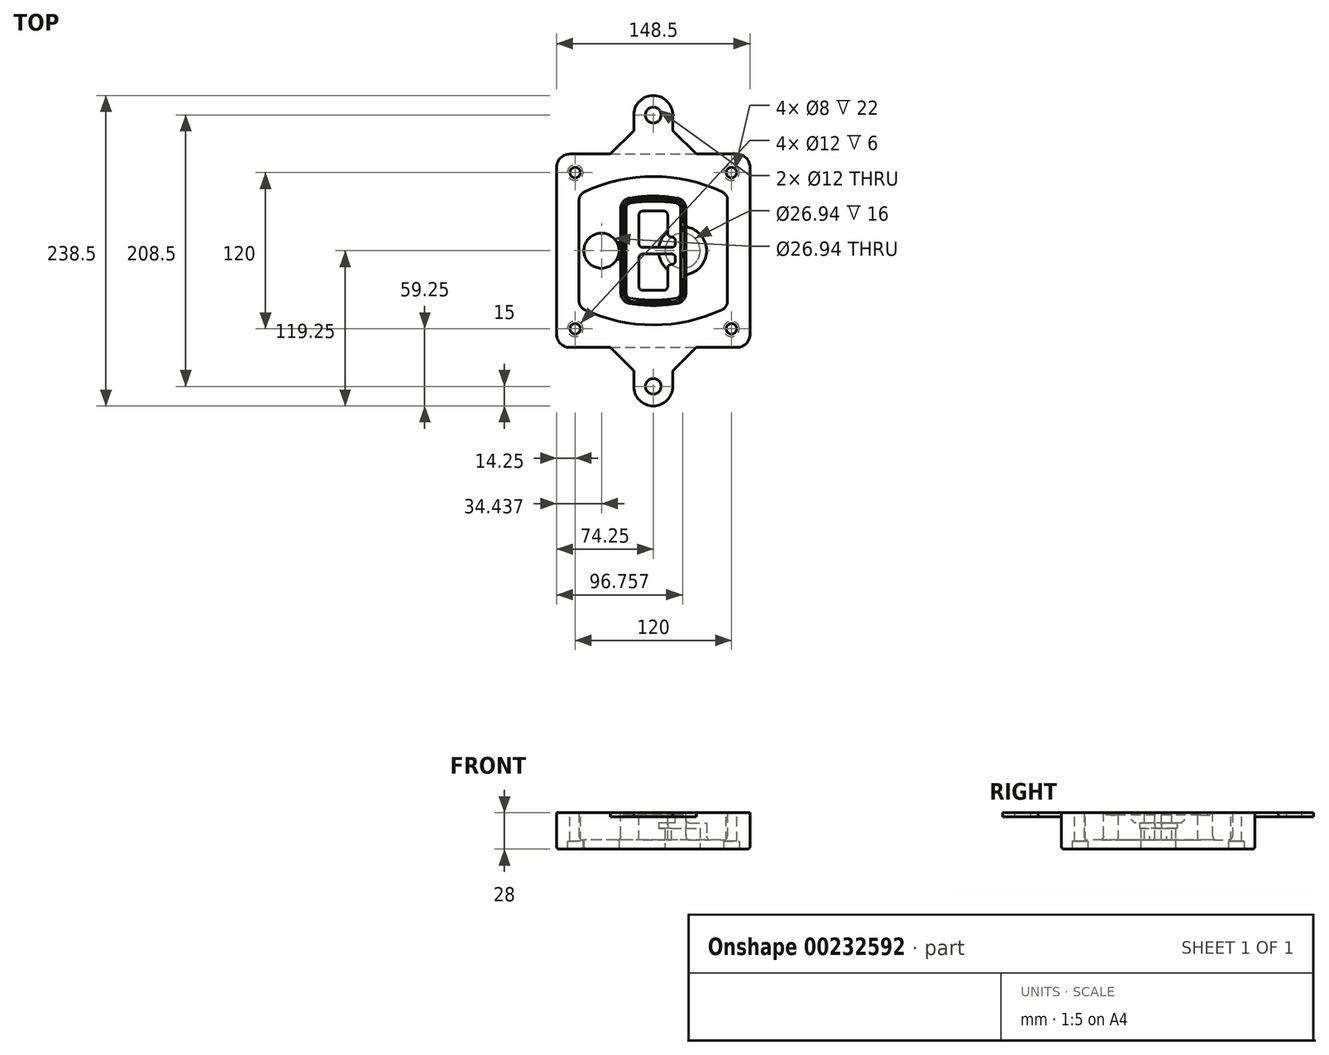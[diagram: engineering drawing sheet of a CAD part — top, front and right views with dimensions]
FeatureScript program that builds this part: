
annotation { "Feature Type Name" : "Feature", "Feature Type Description" : "" }
export const myFeature = defineFeature(function(context is Context, id is Id, definition is map)
    precondition{}
    {
        {
            var Q0;
            Q0=qCreatedBy(makeId("Top.planeOp"),FACE);
            var sketch = newSketch(context, id + "F0", { "sketchPlane" : qUnion([Q0])});
            skPoint(sketch, "E0.rect.middle", {"position": v(0, 0) * mm});
            skLineSegment(sketch, "E1.bottom", {"start": v(-64.25, -74.25) * mm, "end": v(64.25, -74.25) * mm});
            skLineSegment(sketch, "E1.top", {"start": v(-64.25, 74.25) * mm, "end": v(64.25, 74.25) * mm});
            skLineSegment(sketch, "E1.left", {"start": v(-74.25, -64.25) * mm, "end": v(-74.25, 64.25) * mm});
            skLineSegment(sketch, "E1.right", {"start": v(74.25, -64.25) * mm, "end": v(74.25, 64.25) * mm});
            skLineSegment(sketch, "E2", {"start": v(-74.25, 74.25) * mm, "end": v(74.25, -74.25) * mm, "construction": true});
            skLineSegment(sketch, "E3", {"start": v(74.25, 74.25) * mm, "end": v(-74.25, -74.25) * mm, "construction": true});
            skCircle(sketch, "E4", {"center": v(-60, 60) * mm, "radius": 4 * mm});
            skCircle(sketch, "E5", {"center": v(60, 60) * mm, "radius": 4 * mm});
            skCircle(sketch, "E6", {"center": v(60, -60) * mm, "radius": 4 * mm});
            skCircle(sketch, "E7", {"center": v(-60, -60) * mm, "radius": 4 * mm});
            skLineSegment(sketch, "E8", {"start": v(-60, 60) * mm, "end": v(60, 60) * mm, "construction": true});
            skLineSegment(sketch, "E9", {"start": v(60, 60) * mm, "end": v(60, -60) * mm, "construction": true});
            skLineSegment(sketch, "E10", {"start": v(60, -60) * mm, "end": v(-60, -60) * mm, "construction": true});
            skLineSegment(sketch, "E11", {"start": v(-60, -60) * mm, "end": v(-60, 60) * mm, "construction": true});
            skLineSegment(sketch, "E12", {"start": v(-60, 38.83) * mm, "end": v(-60, -38.83) * mm});
            skLineSegment(sketch, "E13", {"start": v(60, 38.83) * mm, "end": v(60, -38.83) * mm});
            skArc(sketch, "E14", {"start": v(54.26, 47.88) * mm, "mid": v(0, 60) * mm, "end": v(-54.26, 47.88) * mm});
            skArc(sketch, "E15", {"start": v(-54.26, -47.88) * mm, "mid": v(0, -60) * mm, "end": v(54.26, -47.88) * mm});
            skLineSegment(sketch, "E16", {"start": v(-60, 0) * mm, "end": v(60, 0) * mm, "construction": true});
            skPoint(sketch, "E17.visualSharp", {"position": v(-60, -45) * mm});
            skArc(sketch, "E17.filletArc", {"start": v(-60, -38.83) * mm, "mid": v(-58.44, -44.2) * mm, "end": v(-54.26, -47.88) * mm});
            skPoint(sketch, "E18.visualSharp", {"position": v(-60, 45) * mm});
            skArc(sketch, "E18.filletArc", {"start": v(-54.26, 47.88) * mm, "mid": v(-58.44, 44.2) * mm, "end": v(-60, 38.83) * mm});
            skPoint(sketch, "E19.visualSharp", {"position": v(60, 45) * mm});
            skArc(sketch, "E19.filletArc", {"start": v(60, 38.83) * mm, "mid": v(58.44, 44.2) * mm, "end": v(54.26, 47.88) * mm});
            skPoint(sketch, "E20.visualSharp", {"position": v(60, -45) * mm});
            skArc(sketch, "E20.filletArc", {"start": v(54.26, -47.88) * mm, "mid": v(58.44, -44.2) * mm, "end": v(60, -38.83) * mm});
            skPoint(sketch, "E21.visualSharp", {"position": v(-74.25, 74.25) * mm});
            skArc(sketch, "E21.filletArc", {"start": v(-64.25, 74.25) * mm, "mid": v(-71.32, 71.32) * mm, "end": v(-74.25, 64.25) * mm});
            skPoint(sketch, "E22.visualSharp", {"position": v(74.25, 74.25) * mm});
            skArc(sketch, "E22.filletArc", {"start": v(74.25, 64.25) * mm, "mid": v(71.32, 71.32) * mm, "end": v(64.25, 74.25) * mm});
            skPoint(sketch, "E23.visualSharp", {"position": v(74.25, -74.25) * mm});
            skArc(sketch, "E23.filletArc", {"start": v(64.25, -74.25) * mm, "mid": v(71.32, -71.32) * mm, "end": v(74.25, -64.25) * mm});
            skPoint(sketch, "E24.visualSharp", {"position": v(-74.25, -74.25) * mm});
            skArc(sketch, "E24.filletArc", {"start": v(-74.25, -64.25) * mm, "mid": v(-71.32, -71.32) * mm, "end": v(-64.25, -74.25) * mm});
            skArc(sketch, "E25.0", {"start": v(57, 38.83) * mm, "mid": v(55.9, 42.58) * mm, "end": v(52.98, 45.17) * mm});
            skLineSegment(sketch, "E25.1", {"start": v(57, 38.83) * mm, "end": v(57, -38.83) * mm});
            skArc(sketch, "E25.2", {"start": v(52.98, -45.17) * mm, "mid": v(55.9, -42.58) * mm, "end": v(57, -38.83) * mm});
            skArc(sketch, "E25.3", {"start": v(-52.98, -45.17) * mm, "mid": v(0, -57) * mm, "end": v(52.98, -45.17) * mm});
            skArc(sketch, "E25.4", {"start": v(-57, -38.83) * mm, "mid": v(-55.9, -42.58) * mm, "end": v(-52.98, -45.17) * mm});
            skArc(sketch, "E25.5", {"start": v(52.98, 45.17) * mm, "mid": v(0, 57) * mm, "end": v(-52.98, 45.17) * mm});
            skLineSegment(sketch, "E25.6", {"start": v(-57, 38.83) * mm, "end": v(-57, -38.83) * mm});
            skArc(sketch, "E25.7", {"start": v(-52.98, 45.17) * mm, "mid": v(-55.9, 42.58) * mm, "end": v(-57, 38.83) * mm});
            skArc(sketch, "E26.0", {"start": v(-55.96, 51.5) * mm, "mid": v(-61.82, 46.33) * mm, "end": v(-64, 38.83) * mm});
            skArc(sketch, "E26.1", {"start": v(55.96, 51.5) * mm, "mid": v(0, 64) * mm, "end": v(-55.96, 51.5) * mm});
            skArc(sketch, "E26.2", {"start": v(64, 38.83) * mm, "mid": v(61.82, 46.33) * mm, "end": v(55.96, 51.5) * mm});
            skLineSegment(sketch, "E26.3", {"start": v(64, 38.83) * mm, "end": v(64, -38.83) * mm});
            skArc(sketch, "E26.4", {"start": v(55.96, -51.5) * mm, "mid": v(61.82, -46.33) * mm, "end": v(64, -38.83) * mm});
            skLineSegment(sketch, "E26.5", {"start": v(-64, 38.83) * mm, "end": v(-64, -38.83) * mm});
            skArc(sketch, "E26.6", {"start": v(-55.96, -51.5) * mm, "mid": v(0, -64) * mm, "end": v(55.96, -51.5) * mm});
            skArc(sketch, "E26.7", {"start": v(-64, -38.83) * mm, "mid": v(-61.82, -46.33) * mm, "end": v(-55.96, -51.5) * mm});
            skSolve(sketch);
        }
        {
            var Q0;
            Q0=makeQuery(id+"F0.imprint","IMPRINT",FACE,{"disambiguationData":[TD([[makeQuery(id+"F0.imprint","IMPRINT",EDGE,{"derivedFrom":sQuery(id+"F0.wireOp",EDGE,"E1.bottom")}),1.0]])]});
            var Q1;
            Q1=makeQuery(id+"F0.imprint","IMPRINT",FACE,{"disambiguationData":[TD([[makeQuery(id+"F0.imprint","IMPRINT",EDGE,{"derivedFrom":sQuery(id+"F0.wireOp",EDGE,"E12")}),1.0]])]});
            var Q2;
            Q2=makeQuery(id+"F0.imprint","IMPRINT",FACE,{"disambiguationData":[TD([[makeQuery(id+"F0.imprint","IMPRINT",EDGE,{"derivedFrom":sQuery(id+"F0.wireOp",EDGE,"E25.0")}),1.0]])]});
            var Q3;
            Q3=makeQuery(id+"F0.imprint","IMPRINT",FACE,{"disambiguationData":[TD([[makeQuery(id+"F0.imprint","IMPRINT",EDGE,{"derivedFrom":sQuery(id+"F0.wireOp",EDGE,"E12")}),-1.0]])]});
            extrude(context, id + "F1", {"entities" : qUnion([Q0, Q1, Q2, Q3]), "oppositeDirection" : true, "depth" : 25 * mm});
        }
        {
            var Q0;
            Q0=makeQuery(id+"F0.imprint","IMPRINT",FACE,{"disambiguationData":[TD([[makeQuery(id+"F0.imprint","IMPRINT",EDGE,{"derivedFrom":sQuery(id+"F0.wireOp",EDGE,"E12")}),1.0]])]});
            extrude(context, id + "F2", {"entities" : qUnion([Q0]), "operationType" : NewBodyOperationType.ADD, "depth" : 3 * mm});
        }
        {
            var Q0;
            Q0=makeQuery(id+"F0.imprint","IMPRINT",FACE,{"disambiguationData":[TD([[makeQuery(id+"F0.imprint","IMPRINT",EDGE,{"derivedFrom":sQuery(id+"F0.wireOp",EDGE,"E25.0")}),1.0]])]});
            extrude(context, id + "F3", {"entities" : qUnion([Q0]), "operationType" : NewBodyOperationType.REMOVE, "oppositeDirection" : true, "depth" : 18 * mm});
        }
        {
            var Q0;
            Q0=makeQuery(id+"F2.opExtrude","CAP_FACE",FACE,{"disambiguationData":[OSD([sQuery(id+"F0.wireOp",EDGE,"E12"),sQuery(id+"F0.wireOp",EDGE,"E13"),sQuery(id+"F0.wireOp",EDGE,"E14"),sQuery(id+"F0.wireOp",EDGE,"E15"),sQuery(id+"F0.wireOp",EDGE,"E17.filletArc"),sQuery(id+"F0.wireOp",EDGE,"E18.filletArc"),sQuery(id+"F0.wireOp",EDGE,"E19.filletArc"),sQuery(id+"F0.wireOp",EDGE,"E20.filletArc"),sQuery(id+"F0.wireOp",EDGE,"E25.0"),sQuery(id+"F0.wireOp",EDGE,"E25.1"),sQuery(id+"F0.wireOp",EDGE,"E25.2"),sQuery(id+"F0.wireOp",EDGE,"E25.3"),sQuery(id+"F0.wireOp",EDGE,"E25.4"),sQuery(id+"F0.wireOp",EDGE,"E25.5"),sQuery(id+"F0.wireOp",EDGE,"E25.6"),sQuery(id+"F0.wireOp",EDGE,"E25.7")])],"isStart":false});
            var sketch = newSketch(context, id + "F4", { "sketchPlane" : qUnion([Q0])});
            skArc(sketch, "E27.0", {"start": v(-18.34, -40.45) * mm, "mid": v(0, -42) * mm, "end": v(18.34, -40.45) * mm});
            skArc(sketch, "E28.0", {"start": v(18.34, 40.45) * mm, "mid": v(0, 42) * mm, "end": v(-18.34, 40.45) * mm});
            skLineSegment(sketch, "E29", {"start": v(-25, 32.57) * mm, "end": v(-25, -32.57) * mm});
            skLineSegment(sketch, "E30", {"start": v(25, 32.57) * mm, "end": v(25, -32.57) * mm});
            skLineSegment(sketch, "E31", {"start": v(-25, 39.1) * mm, "end": v(25, 39.1) * mm, "construction": true});
            skLineSegment(sketch, "E32", {"start": v(-25, -39.1) * mm, "end": v(25, -39.1) * mm, "construction": true});
            skPoint(sketch, "E33.visualSharp", {"position": v(-25, 39.1) * mm});
            skArc(sketch, "E33.filletArc", {"start": v(-18.34, 40.45) * mm, "mid": v(-23.11, 37.73) * mm, "end": v(-25, 32.57) * mm});
            skPoint(sketch, "E34.visualSharp", {"position": v(25, 39.1) * mm});
            skArc(sketch, "E34.filletArc", {"start": v(25, 32.57) * mm, "mid": v(23.11, 37.73) * mm, "end": v(18.34, 40.45) * mm});
            skPoint(sketch, "E35.visualSharp", {"position": v(25, -39.1) * mm});
            skArc(sketch, "E35.filletArc", {"start": v(18.34, -40.45) * mm, "mid": v(23.11, -37.73) * mm, "end": v(25, -32.57) * mm});
            skPoint(sketch, "E36.visualSharp", {"position": v(-25, -39.1) * mm});
            skArc(sketch, "E36.filletArc", {"start": v(-25, -32.57) * mm, "mid": v(-23.11, -37.73) * mm, "end": v(-18.34, -40.45) * mm});
            skArc(sketch, "E37.0", {"start": v(52.98, 45.17) * mm, "mid": v(0, 57) * mm, "end": v(-52.98, 45.17) * mm});
            skArc(sketch, "E37.1", {"start": v(-52.98, 45.17) * mm, "mid": v(-55.9, 42.58) * mm, "end": v(-57, 38.83) * mm});
            skLineSegment(sketch, "E37.2", {"start": v(-57, 38.83) * mm, "end": v(-57, -38.83) * mm});
            skArc(sketch, "E37.3", {"start": v(-57, -38.83) * mm, "mid": v(-55.9, -42.58) * mm, "end": v(-52.98, -45.17) * mm});
            skArc(sketch, "E37.4", {"start": v(-52.98, -45.17) * mm, "mid": v(0, -57) * mm, "end": v(52.98, -45.17) * mm});
            skArc(sketch, "E37.5", {"start": v(52.98, -45.17) * mm, "mid": v(55.9, -42.58) * mm, "end": v(57, -38.83) * mm});
            skLineSegment(sketch, "E37.6", {"start": v(57, 38.83) * mm, "end": v(57, -38.83) * mm});
            skArc(sketch, "E37.7", {"start": v(57, 38.83) * mm, "mid": v(55.9, 42.58) * mm, "end": v(52.98, 45.17) * mm});
            skLineSegment(sketch, "E38.0", {"start": v(23, 32.57) * mm, "end": v(23, -32.57) * mm});
            skArc(sketch, "E38.1", {"start": v(18, -38.48) * mm, "mid": v(21.58, -36.44) * mm, "end": v(23, -32.57) * mm});
            skArc(sketch, "E38.2", {"start": v(-18, -38.48) * mm, "mid": v(0, -40) * mm, "end": v(18, -38.48) * mm});
            skArc(sketch, "E38.3", {"start": v(-23, -32.57) * mm, "mid": v(-21.58, -36.44) * mm, "end": v(-18, -38.48) * mm});
            skLineSegment(sketch, "E38.4", {"start": v(-23, 32.57) * mm, "end": v(-23, -32.57) * mm});
            skArc(sketch, "E38.5", {"start": v(23, 32.57) * mm, "mid": v(21.58, 36.44) * mm, "end": v(18, 38.48) * mm});
            skArc(sketch, "E38.6", {"start": v(-18, 38.48) * mm, "mid": v(-21.58, 36.44) * mm, "end": v(-23, 32.57) * mm});
            skArc(sketch, "E38.7", {"start": v(18, 38.48) * mm, "mid": v(0, 40) * mm, "end": v(-18, 38.48) * mm});
            skArc(sketch, "E39.0", {"start": v(21, 32.57) * mm, "mid": v(20.06, 35.15) * mm, "end": v(17.67, 36.5) * mm});
            skLineSegment(sketch, "E39.1", {"start": v(21, 32.57) * mm, "end": v(21, -32.57) * mm});
            skArc(sketch, "E39.2", {"start": v(17.67, -36.5) * mm, "mid": v(20.06, -35.15) * mm, "end": v(21, -32.57) * mm});
            skArc(sketch, "E39.3", {"start": v(-17.67, -36.5) * mm, "mid": v(0, -38) * mm, "end": v(17.67, -36.5) * mm});
            skArc(sketch, "E39.4", {"start": v(-21, -32.57) * mm, "mid": v(-20.06, -35.15) * mm, "end": v(-17.67, -36.5) * mm});
            skArc(sketch, "E39.5", {"start": v(17.67, 36.5) * mm, "mid": v(0, 38) * mm, "end": v(-17.67, 36.5) * mm});
            skLineSegment(sketch, "E39.6", {"start": v(-21, 32.57) * mm, "end": v(-21, -32.57) * mm});
            skArc(sketch, "E39.7", {"start": v(-17.67, 36.5) * mm, "mid": v(-20.06, 35.15) * mm, "end": v(-21, 32.57) * mm});
            skLineSegment(sketch, "E40", {"start": v(-25, 0) * mm, "end": v(25, 0) * mm, "construction": true});
            skLineSegment(sketch, "E41", {"start": v(-11, 5.5) * mm, "end": v(-11, 27.5) * mm});
            skLineSegment(sketch, "E42", {"start": v(-8, 30.5) * mm, "end": v(8, 30.5) * mm});
            skLineSegment(sketch, "E43", {"start": v(11, 27.5) * mm, "end": v(11, 13.5) * mm});
            skLineSegment(sketch, "E44", {"start": v(14, 10.5) * mm, "end": v(14, 10.5) * mm});
            skLineSegment(sketch, "E45", {"start": v(17, 7.5) * mm, "end": v(17, 5.5) * mm});
            skLineSegment(sketch, "E46", {"start": v(14, 2.5) * mm, "end": v(-8, 2.5) * mm});
            skPoint(sketch, "E47.visualSharp", {"position": v(-11, 30.5) * mm});
            skArc(sketch, "E47.filletArc", {"start": v(-8, 30.5) * mm, "mid": v(-10.12, 29.62) * mm, "end": v(-11, 27.5) * mm});
            skPoint(sketch, "E48.visualSharp", {"position": v(11, 30.5) * mm});
            skArc(sketch, "E48.filletArc", {"start": v(11, 27.5) * mm, "mid": v(10.12, 29.62) * mm, "end": v(8, 30.5) * mm});
            skPoint(sketch, "E49.visualSharp", {"position": v(11, 10.5) * mm});
            skArc(sketch, "E49.filletArc", {"start": v(11, 13.5) * mm, "mid": v(11.88, 11.38) * mm, "end": v(14, 10.5) * mm});
            skPoint(sketch, "E50.visualSharp", {"position": v(17, 10.5) * mm});
            skArc(sketch, "E50.filletArc", {"start": v(17, 7.5) * mm, "mid": v(16.12, 9.62) * mm, "end": v(14, 10.5) * mm});
            skPoint(sketch, "E51.visualSharp", {"position": v(17, 2.5) * mm});
            skArc(sketch, "E51.filletArc", {"start": v(14, 2.5) * mm, "mid": v(16.12, 3.38) * mm, "end": v(17, 5.5) * mm});
            skPoint(sketch, "E52.visualSharp", {"position": v(-11, 2.5) * mm});
            skArc(sketch, "E52.filletArc", {"start": v(-11, 5.5) * mm, "mid": v(-10.12, 3.38) * mm, "end": v(-8, 2.5) * mm});
            skLineSegment(sketch, "E53.0.MirrorCS", {"start": v(14, -2.5) * mm, "end": v(-8, -2.5) * mm});
            skArc(sketch, "E54.0.MirrorCS", {"start": v(-11, -5.5) * mm, "mid": v(-10.12, -3.38) * mm, "end": v(-8, -2.5) * mm});
            skLineSegment(sketch, "E55.0.MirrorCS", {"start": v(-11, -5.5) * mm, "end": v(-11, -27.5) * mm});
            skArc(sketch, "E56.0.MirrorCS", {"start": v(-8, -30.5) * mm, "mid": v(-10.12, -29.62) * mm, "end": v(-11, -27.5) * mm});
            skLineSegment(sketch, "E57.0.MirrorCS", {"start": v(-8, -30.5) * mm, "end": v(8, -30.5) * mm});
            skArc(sketch, "E58.0.MirrorCS", {"start": v(11, -27.5) * mm, "mid": v(10.12, -29.62) * mm, "end": v(8, -30.5) * mm});
            skLineSegment(sketch, "E59.0.MirrorCS", {"start": v(11, -27.5) * mm, "end": v(11, -13.5) * mm});
            skArc(sketch, "E60.0.MirrorCS", {"start": v(11, -13.5) * mm, "mid": v(11.88, -11.38) * mm, "end": v(14, -10.5) * mm});
            skArc(sketch, "E61.0.MirrorCS", {"start": v(17, -7.5) * mm, "mid": v(16.12, -9.62) * mm, "end": v(14, -10.5) * mm});
            skLineSegment(sketch, "E62.0.MirrorCS", {"start": v(17, -7.5) * mm, "end": v(17, -5.5) * mm});
            skArc(sketch, "E63.0.MirrorCS", {"start": v(14, -2.5) * mm, "mid": v(16.12, -3.38) * mm, "end": v(17, -5.5) * mm});
            skSolve(sketch);
        }
        {
            var Q0;
            Q0=makeQuery(id+"F4.imprint","IMPRINT",FACE,{"disambiguationData":[TD([[makeQuery(id+"F4.imprint","IMPRINT",EDGE,{"derivedFrom":sQuery(id+"F4.wireOp",EDGE,"E27.0")}),1.0]])]});
            var Q1;
            Q1=makeQuery(id+"F4.imprint","IMPRINT",FACE,{"disambiguationData":[TD([[makeQuery(id+"F4.imprint","IMPRINT",EDGE,{"derivedFrom":sQuery(id+"F4.wireOp",EDGE,"E38.0")}),-1.0]])]});
            var Q2;
            Q2=makeQuery(id+"F4.imprint","IMPRINT",FACE,{"disambiguationData":[TD([[makeQuery(id+"F4.imprint","IMPRINT",EDGE,{"derivedFrom":sQuery(id+"F4.wireOp",EDGE,"E39.0")}),1.0]])]});
            extrude(context, id + "F5", {"entities" : qUnion([Q0, Q1, Q2]), "operationType" : NewBodyOperationType.ADD, "endBound" : BoundingType.UP_TO_NEXT, "oppositeDirection" : true, "depth" : 25 * mm});
        }
        {
            var Q0;
            Q0=makeQuery(id+"F4.imprint","IMPRINT",FACE,{"disambiguationData":[TD([[makeQuery(id+"F4.imprint","IMPRINT",EDGE,{"derivedFrom":sQuery(id+"F4.wireOp",EDGE,"E38.0")}),-1.0]])]});
            extrude(context, id + "F6", {"entities" : qUnion([Q0]), "operationType" : NewBodyOperationType.REMOVE, "oppositeDirection" : true, "depth" : 2 * mm});
        }
        {
            var Q0;
            Q0=makeQuery(id+"F1.opExtrude","CAP_FACE",FACE,{"disambiguationData":[OSD([sQuery(id+"F0.wireOp",EDGE,"E1.bottom"),sQuery(id+"F0.wireOp",EDGE,"E1.top"),sQuery(id+"F0.wireOp",EDGE,"E1.left"),sQuery(id+"F0.wireOp",EDGE,"E1.right"),sQuery(id+"F0.wireOp",EDGE,"E4"),sQuery(id+"F0.wireOp",EDGE,"E5"),sQuery(id+"F0.wireOp",EDGE,"E6"),sQuery(id+"F0.wireOp",EDGE,"E7"),sQuery(id+"F0.wireOp",EDGE,"E21.filletArc"),sQuery(id+"F0.wireOp",EDGE,"E22.filletArc"),sQuery(id+"F0.wireOp",EDGE,"E23.filletArc"),sQuery(id+"F0.wireOp",EDGE,"E24.filletArc")])],"isStart":false});
            var sketch = newSketch(context, id + "F7", { "sketchPlane" : qUnion([Q0])});
            skCircle(sketch, "E64", {"center": v(22.5, 0) * mm, "radius": 13.47 * mm});
            skCircle(sketch, "E65", {"center": v(-39.81, 0) * mm, "radius": 13.47 * mm});
            skLineSegment(sketch, "E66", {"start": v(74.25, 0) * mm, "end": v(-74.25, 0) * mm});
            skCircle(sketch, "E67", {"center": v(22.5, 0) * mm, "radius": 18.47 * mm});
            skCircle(sketch, "E68", {"center": v(60, -60) * mm, "radius": 6 * mm});
            skCircle(sketch, "E69", {"center": v(-60, -60) * mm, "radius": 6 * mm});
            skCircle(sketch, "E70", {"center": v(-60, 60) * mm, "radius": 6 * mm});
            skCircle(sketch, "E71", {"center": v(60, 60) * mm, "radius": 6 * mm});
            skSolve(sketch);
        }
        {
            var Q0;
            {var subQ1=sQuery(id+"F7.wireOp",EDGE,"E66");var subQ4=sQuery(id+"F7.wireOp",EDGE,"E64");var subQ6=makeQuery(id+"F7.imprint","INTERSECT",VERTEX,{"disambiguationData":[OD(0.0)],"derivedFrom":[subQ4,subQ1]});Q0=makeQuery(id+"F7.imprint","IMPRINT",FACE,{"disambiguationData":[TD([[makeQuery(id+"F7.imprint","IMPRINT",EDGE,{"disambiguationData":[TD([[subQ6,-1.0]])],"derivedFrom":subQ4}),-1.0]])]});}
            var Q1;
            {var subQ0=sQuery(id+"F7.wireOp",EDGE,"E66");var subQ1=sQuery(id+"F7.wireOp",EDGE,"E64");var subQ3=makeQuery(id+"F7.imprint","INTERSECT",VERTEX,{"disambiguationData":[OD(0.0)],"derivedFrom":[subQ1,subQ0]});Q1=makeQuery(id+"F7.imprint","IMPRINT",FACE,{"disambiguationData":[TD([[makeQuery(id+"F7.imprint","IMPRINT",EDGE,{"disambiguationData":[TD([[subQ3,-1.0]])],"derivedFrom":subQ1}),1.0]])]});}
            var Q2;
            {var subQ0=sQuery(id+"F7.wireOp",EDGE,"E66");var subQ1=sQuery(id+"F7.wireOp",EDGE,"E64");var subQ3=makeQuery(id+"F7.imprint","INTERSECT",VERTEX,{"disambiguationData":[OD(0.0)],"derivedFrom":[subQ1,subQ0]});Q2=makeQuery(id+"F7.imprint","IMPRINT",FACE,{"disambiguationData":[TD([[makeQuery(id+"F7.imprint","IMPRINT",EDGE,{"disambiguationData":[TD([[subQ3,1.0]])],"derivedFrom":subQ1}),1.0]])]});}
            var Q3;
            {var subQ1=sQuery(id+"F7.wireOp",EDGE,"E66");var subQ4=sQuery(id+"F7.wireOp",EDGE,"E64");var subQ6=makeQuery(id+"F7.imprint","INTERSECT",VERTEX,{"disambiguationData":[OD(0.0)],"derivedFrom":[subQ4,subQ1]});Q3=makeQuery(id+"F7.imprint","IMPRINT",FACE,{"disambiguationData":[TD([[makeQuery(id+"F7.imprint","IMPRINT",EDGE,{"disambiguationData":[TD([[subQ6,1.0]])],"derivedFrom":subQ4}),-1.0]])]});}
            extrude(context, id + "F8", {"entities" : qUnion([Q0, Q1, Q2, Q3]), "operationType" : NewBodyOperationType.ADD, "oppositeDirection" : true, "depth" : 20 * mm});
        }
        {
            var Q0;
            {var subQ0=sQuery(id+"F7.wireOp",EDGE,"E66");var subQ1=sQuery(id+"F7.wireOp",EDGE,"E64");var subQ3=makeQuery(id+"F7.imprint","INTERSECT",VERTEX,{"disambiguationData":[OD(0.0)],"derivedFrom":[subQ1,subQ0]});Q0=makeQuery(id+"F7.imprint","IMPRINT",FACE,{"disambiguationData":[TD([[makeQuery(id+"F7.imprint","IMPRINT",EDGE,{"disambiguationData":[TD([[subQ3,-1.0]])],"derivedFrom":subQ1}),1.0]])]});}
            var Q1;
            {var subQ0=sQuery(id+"F7.wireOp",EDGE,"E66");var subQ1=sQuery(id+"F7.wireOp",EDGE,"E64");var subQ3=makeQuery(id+"F7.imprint","INTERSECT",VERTEX,{"disambiguationData":[OD(0.0)],"derivedFrom":[subQ1,subQ0]});Q1=makeQuery(id+"F7.imprint","IMPRINT",FACE,{"disambiguationData":[TD([[makeQuery(id+"F7.imprint","IMPRINT",EDGE,{"disambiguationData":[TD([[subQ3,1.0]])],"derivedFrom":subQ1}),1.0]])]});}
            extrude(context, id + "F9", {"entities" : qUnion([Q0, Q1]), "operationType" : NewBodyOperationType.REMOVE, "oppositeDirection" : true, "depth" : 16 * mm});
        }
        {
            var Q0;
            {var subQ0=sQuery(id+"F7.wireOp",EDGE,"E66");var subQ1=sQuery(id+"F7.wireOp",EDGE,"E65");var subQ3=makeQuery(id+"F7.imprint","INTERSECT",VERTEX,{"disambiguationData":[OD(0.0)],"derivedFrom":[subQ1,subQ0]});Q0=makeQuery(id+"F7.imprint","IMPRINT",FACE,{"disambiguationData":[TD([[makeQuery(id+"F7.imprint","IMPRINT",EDGE,{"disambiguationData":[TD([[subQ3,-1.0]])],"derivedFrom":subQ1}),1.0]])]});}
            var Q1;
            {var subQ0=sQuery(id+"F7.wireOp",EDGE,"E66");var subQ1=sQuery(id+"F7.wireOp",EDGE,"E65");var subQ3=makeQuery(id+"F7.imprint","INTERSECT",VERTEX,{"disambiguationData":[OD(0.0)],"derivedFrom":[subQ1,subQ0]});Q1=makeQuery(id+"F7.imprint","IMPRINT",FACE,{"disambiguationData":[TD([[makeQuery(id+"F7.imprint","IMPRINT",EDGE,{"disambiguationData":[TD([[subQ3,1.0]])],"derivedFrom":subQ1}),1.0]])]});}
            extrude(context, id + "F10", {"entities" : qUnion([Q0, Q1]), "operationType" : NewBodyOperationType.REMOVE, "oppositeDirection" : true, "depth" : 25 * mm});
        }
        {
            var Q0;
            Q0=makeQuery(id+"F7.imprint","IMPRINT",FACE,{"disambiguationData":[TD([[makeQuery(id+"F7.imprint","IMPRINT",EDGE,{"derivedFrom":sQuery(id+"F7.wireOp",EDGE,"E68")}),1.0]])]});
            var Q1;
            Q1=makeQuery(id+"F7.imprint","IMPRINT",FACE,{"disambiguationData":[TD([[makeQuery(id+"F7.imprint","IMPRINT",EDGE,{"derivedFrom":makeQuery(id+"F1.opExtrude","CAP_EDGE",EDGE,{"disambiguationData":[OSD([sQuery(id+"F0.wireOp",EDGE,"E5")])],"isStart":false})}),-1.0]])]});
            var Q2;
            Q2=makeQuery(id+"F7.imprint","IMPRINT",FACE,{"disambiguationData":[TD([[makeQuery(id+"F7.imprint","IMPRINT",EDGE,{"derivedFrom":sQuery(id+"F7.wireOp",EDGE,"E69")}),1.0]])]});
            var Q3;
            Q3=makeQuery(id+"F7.imprint","IMPRINT",FACE,{"disambiguationData":[TD([[makeQuery(id+"F7.imprint","IMPRINT",EDGE,{"derivedFrom":makeQuery(id+"F1.opExtrude","CAP_EDGE",EDGE,{"disambiguationData":[OSD([sQuery(id+"F0.wireOp",EDGE,"E4")])],"isStart":false})}),-1.0]])]});
            var Q4;
            Q4=makeQuery(id+"F7.imprint","IMPRINT",FACE,{"disambiguationData":[TD([[makeQuery(id+"F7.imprint","IMPRINT",EDGE,{"derivedFrom":sQuery(id+"F7.wireOp",EDGE,"E70")}),1.0]])]});
            var Q5;
            Q5=makeQuery(id+"F7.imprint","IMPRINT",FACE,{"disambiguationData":[TD([[makeQuery(id+"F7.imprint","IMPRINT",EDGE,{"derivedFrom":makeQuery(id+"F1.opExtrude","CAP_EDGE",EDGE,{"disambiguationData":[OSD([sQuery(id+"F0.wireOp",EDGE,"E7")])],"isStart":false})}),-1.0]])]});
            var Q6;
            Q6=makeQuery(id+"F7.imprint","IMPRINT",FACE,{"disambiguationData":[TD([[makeQuery(id+"F7.imprint","IMPRINT",EDGE,{"derivedFrom":sQuery(id+"F7.wireOp",EDGE,"E71")}),1.0]])]});
            var Q7;
            Q7=makeQuery(id+"F7.imprint","IMPRINT",FACE,{"disambiguationData":[TD([[makeQuery(id+"F7.imprint","IMPRINT",EDGE,{"derivedFrom":makeQuery(id+"F1.opExtrude","CAP_EDGE",EDGE,{"disambiguationData":[OSD([sQuery(id+"F0.wireOp",EDGE,"E6")])],"isStart":false})}),-1.0]])]});
            extrude(context, id + "F11", {"entities" : qUnion([Q0, Q1, Q2, Q3, Q4, Q5, Q6, Q7]), "operationType" : NewBodyOperationType.REMOVE, "oppositeDirection" : true, "depth" : 6 * mm});
        }
        {
            var Q0;
            Q0=makeQuery(id+"F9.boolean.opBoolean","COPY",FACE,{"derivedFrom":makeQuery(id+"F9.opExtrude","CAP_FACE",FACE,{"disambiguationData":[OSD([sQuery(id+"F7.wireOp",EDGE,"E64")])],"isStart":false})});
            var sketch = newSketch(context, id + "F12", { "sketchPlane" : qUnion([Q0])});
            skArc(sketch, "E72.0", {"start": v(11, 14.45) * mm, "mid": v(6.45, 9.13) * mm, "end": v(4.2, 2.5) * mm});
            skArc(sketch, "E72.1", {"start": v(4.2, -2.5) * mm, "mid": v(6.45, -9.13) * mm, "end": v(11, -14.45) * mm});
            skLineSegment(sketch, "E73", {"start": v(4.2, -2.5) * mm, "end": v(14, -2.5) * mm});
            skLineSegment(sketch, "E74.0", {"start": v(14, 2.5) * mm, "end": v(4.2, 2.5) * mm});
            skArc(sketch, "E74.1", {"start": v(14, 2.5) * mm, "mid": v(16.12, 3.38) * mm, "end": v(17, 5.5) * mm});
            skLineSegment(sketch, "E74.2", {"start": v(17, 7.5) * mm, "end": v(17, 5.5) * mm});
            skArc(sketch, "E74.3", {"start": v(17, 7.5) * mm, "mid": v(16.12, 9.62) * mm, "end": v(14, 10.5) * mm});
            skArc(sketch, "E74.4", {"start": v(11, 13.5) * mm, "mid": v(11.88, 11.38) * mm, "end": v(14, 10.5) * mm});
            skLineSegment(sketch, "E74.5", {"start": v(11, 14.45) * mm, "end": v(11, 13.5) * mm});
            skLineSegment(sketch, "E74.7", {"start": v(14, -2.5) * mm, "end": v(4.2, -2.5) * mm});
            skArc(sketch, "E74.8", {"start": v(14, -2.5) * mm, "mid": v(16.12, -3.38) * mm, "end": v(17, -5.5) * mm});
            skLineSegment(sketch, "E74.9", {"start": v(17, -7.5) * mm, "end": v(17, -5.5) * mm});
            skArc(sketch, "E74.10", {"start": v(17, -7.5) * mm, "mid": v(16.12, -9.62) * mm, "end": v(14, -10.5) * mm});
            skArc(sketch, "E74.11", {"start": v(11, -13.5) * mm, "mid": v(11.88, -11.38) * mm, "end": v(14, -10.5) * mm});
            skLineSegment(sketch, "E74.12", {"start": v(11, -14.45) * mm, "end": v(11, -13.5) * mm});
            skPoint(sketch, "E75.orphan", {"position": v(11, -27.5) * mm});
            skPoint(sketch, "E76.orphan", {"position": v(-8, -2.5) * mm});
            skPoint(sketch, "E77.orphan", {"position": v(-8, 2.5) * mm});
            skPoint(sketch, "E78.orphan", {"position": v(11, 27.5) * mm});
            skSolve(sketch);
        }
        {
            var Q0;
            {var subQ7=sQuery(id+"F12.wireOp",EDGE,"E72.0");var subQ14=sQuery(id+"F12.wireOp",EDGE,"E72.1");var subQ16=sQuery(id+"F12.wireOp",EDGE,"E74.1");var subQ18=sQuery(id+"F12.wireOp",EDGE,"E74.8");Q0=qUnion([makeQuery(id+"F12.imprint","IMPRINT",FACE,{"disambiguationData":[TD([[makeQuery(id+"F12.imprint","IMPRINT",EDGE,{"derivedFrom":subQ7}),1.0]])]}),makeQuery(id+"F12.imprint","IMPRINT",FACE,{"disambiguationData":[TD([[makeQuery(id+"F12.imprint","IMPRINT",EDGE,{"derivedFrom":subQ14}),1.0]])]}),makeQuery(id+"F12.imprint","IMPRINT",FACE,{"disambiguationData":[TD([[makeQuery(id+"F12.imprint","IMPRINT",EDGE,{"derivedFrom":subQ16}),1.0]])]}),makeQuery(id+"F12.imprint","IMPRINT",FACE,{"disambiguationData":[TD([[makeQuery(id+"F12.imprint","IMPRINT",EDGE,{"derivedFrom":subQ18}),-1.0]])]})]);}
            var Q1;
            Q1=makeQuery(id+"F5.boolean.opBoolean","SPLIT",FACE,{"disambiguationData":[TD([makeQuery(id+"F5.opExtrude","SWEPT_FACE",FACE,{"disambiguationData":[OSD([sQuery(id+"F4.wireOp",EDGE,"E41")])]})])],"derivedFrom":makeQuery(id+"F3.boolean.opBoolean","COPY",FACE,{"derivedFrom":makeQuery(id+"F3.opExtrude","CAP_FACE",FACE,{"disambiguationData":[OSD([sQuery(id+"F0.wireOp",EDGE,"E25.0"),sQuery(id+"F0.wireOp",EDGE,"E25.1"),sQuery(id+"F0.wireOp",EDGE,"E25.2"),sQuery(id+"F0.wireOp",EDGE,"E25.3"),sQuery(id+"F0.wireOp",EDGE,"E25.4"),sQuery(id+"F0.wireOp",EDGE,"E25.5"),sQuery(id+"F0.wireOp",EDGE,"E25.6"),sQuery(id+"F0.wireOp",EDGE,"E25.7")])],"isStart":false})})});
            extrude(context, id + "F13", {"entities" : qUnion([Q0]), "operationType" : NewBodyOperationType.REMOVE, "endBound" : BoundingType.UP_TO_SURFACE, "endBoundEntityFace" : qUnion([Q1]), "depth" : 25 * mm});
        }
        {
            var Q0;
            Q0=makeQuery(id+"F3.boolean.opBoolean","COPY",EDGE,{"derivedFrom":makeQuery(id+"F3.opExtrude","CAP_EDGE",EDGE,{"disambiguationData":[OSD([sQuery(id+"F0.wireOp",EDGE,"E25.6")])],"isStart":false})});
            var Q1;
            Q1=makeQuery(id+"F8.boolean.opBoolean","INTERSECT",EDGE,{"derivedFrom":[makeQuery(id+"F5.opExtrude","SWEPT_FACE",FACE,{"disambiguationData":[OSD([sQuery(id+"F4.wireOp",EDGE,"E30")])]}),makeQuery(id+"F8.opExtrude","CAP_FACE",FACE,{"disambiguationData":[OSD([sQuery(id+"F7.wireOp",EDGE,"E67")])],"isStart":false})]});
            var Q2;
            Q2=makeQuery(id+"F8.boolean.opBoolean","INTERSECT",EDGE,{"disambiguationData":[OD(1.0)],"derivedFrom":[makeQuery(id+"F5.opExtrude","SWEPT_FACE",FACE,{"disambiguationData":[OSD([sQuery(id+"F4.wireOp",EDGE,"E30")])]}),makeQuery(id+"F8.opExtrude","SWEPT_FACE",FACE,{"disambiguationData":[OSD([sQuery(id+"F7.wireOp",EDGE,"E67")])]})]});
            var Q3;
            {var subQ0=sQuery(id+"F4.wireOp",EDGE,"E30");Q3=makeQuery(id+"F8.boolean.opBoolean","SPLIT",EDGE,{"disambiguationData":[TD([makeQuery(id+"F5.opExtrude","SWEPT_FACE",FACE,{"disambiguationData":[OSD([sQuery(id+"F4.wireOp",EDGE,"E35.filletArc")])]})])],"derivedFrom":makeQuery(id+"F5.opExtrude","CAP_EDGE",EDGE,{"disambiguationData":[OSD([subQ0])],"isStart":false})});}
            var Q4;
            {var subQ0=sQuery(id+"F0.wireOp",EDGE,"E25.7");var subQ1=sQuery(id+"F0.wireOp",EDGE,"E25.1");var subQ2=sQuery(id+"F0.wireOp",EDGE,"E25.6");var subQ3=sQuery(id+"F0.wireOp",EDGE,"E25.5");var subQ4=sQuery(id+"F0.wireOp",EDGE,"E25.4");var subQ5=sQuery(id+"F0.wireOp",EDGE,"E25.0");var subQ6=sQuery(id+"F0.wireOp",EDGE,"E25.2");var subQ7=sQuery(id+"F0.wireOp",EDGE,"E25.3");Q4=makeQuery(id+"F8.boolean.opBoolean","INTERSECT",EDGE,{"derivedFrom":[makeQuery(id+"F5.boolean.opBoolean","SPLIT",FACE,{"disambiguationData":[TD([makeQuery(id+"F2.opExtrude","SWEPT_FACE",FACE,{"disambiguationData":[OSD([subQ5])]})])],"derivedFrom":makeQuery(id+"F3.boolean.opBoolean","COPY",FACE,{"derivedFrom":makeQuery(id+"F3.opExtrude","CAP_FACE",FACE,{"disambiguationData":[OSD([subQ5,subQ1,subQ6,subQ7,subQ4,subQ3,subQ2,subQ0])],"isStart":false})})}),makeQuery(id+"F8.opExtrude","SWEPT_FACE",FACE,{"disambiguationData":[OSD([sQuery(id+"F7.wireOp",EDGE,"E67")])]})]});}
            var Q5;
            Q5=makeQuery(id+"F8.boolean.opBoolean","INTERSECT",EDGE,{"disambiguationData":[OD(0.0)],"derivedFrom":[makeQuery(id+"F5.opExtrude","SWEPT_FACE",FACE,{"disambiguationData":[OSD([sQuery(id+"F4.wireOp",EDGE,"E30")])]}),makeQuery(id+"F8.opExtrude","SWEPT_FACE",FACE,{"disambiguationData":[OSD([sQuery(id+"F7.wireOp",EDGE,"E67")])]})]});
            fillet(context, id + "F14", {"entities" : qUnion([Q0, Q1, Q2, Q3, Q4, Q5]), "radius" : 3 * mm, "tangentPropagation" : true, "allowEdgeOverflow" : false});
        }
        {
            var Q0;
            Q0=makeQuery(id+"F1.opExtrude","CAP_EDGE",EDGE,{"disambiguationData":[OSD([sQuery(id+"F0.wireOp",EDGE,"E1.bottom")])],"isStart":false});
            fillet(context, id + "F15", {"entities" : qUnion([Q0]), "radius" : 2 * mm, "tangentPropagation" : true, "allowEdgeOverflow" : false});
        }
        {
            var Q0;
            {var subQ0=sQuery(id+"F0.wireOp",EDGE,"E22.filletArc");var subQ1=sQuery(id+"F0.wireOp",EDGE,"E7");var subQ2=sQuery(id+"F0.wireOp",EDGE,"E6");var subQ3=sQuery(id+"F0.wireOp",EDGE,"E5");var subQ4=sQuery(id+"F0.wireOp",EDGE,"E4");var subQ5=sQuery(id+"F0.wireOp",EDGE,"E1.bottom");var subQ6=sQuery(id+"F0.wireOp",EDGE,"E21.filletArc");var subQ7=sQuery(id+"F0.wireOp",EDGE,"E1.top");var subQ8=sQuery(id+"F0.wireOp",EDGE,"E1.left");var subQ9=sQuery(id+"F0.wireOp",EDGE,"E1.right");var subQ10=sQuery(id+"F0.wireOp",EDGE,"E23.filletArc");var subQ11=sQuery(id+"F0.wireOp",EDGE,"E24.filletArc");Q0=makeQuery(id+"F2.boolean.opBoolean","SPLIT",FACE,{"disambiguationData":[TD([makeQuery(id+"F1.opExtrude","SWEPT_FACE",FACE,{"disambiguationData":[OSD([subQ5])]})])],"derivedFrom":makeQuery(id+"F1.opExtrude","CAP_FACE",FACE,{"disambiguationData":[OSD([subQ5,subQ7,subQ8,subQ9,subQ4,subQ3,subQ2,subQ1,subQ6,subQ0,subQ10,subQ11])],"isStart":true})});}
            var sketch = newSketch(context, id + "F16", { "sketchPlane" : qUnion([Q0])});
            skSolve(sketch);
        }
        {
            var Q0;
            Q0=makeQuery(id+"F16.imprint","IMPRINT",FACE,{"disambiguationData":[TD([[makeQuery(id+"F16.imprint","IMPRINT",EDGE,{"derivedFrom":makeQuery(id+"F1.opExtrude","CAP_EDGE",EDGE,{"disambiguationData":[OSD([sQuery(id+"F0.wireOp",EDGE,"E1.bottom")])],"isStart":true})}),1.0]])]});
            var sketch = newSketch(context, id + "F17", { "sketchPlane" : qUnion([Q0])});
            skLineSegment(sketch, "E79", {"start": v(0, 74.25) * mm, "end": v(0, 104.25) * mm, "construction": true});
            skCircle(sketch, "E80", {"center": v(0, 104.25) * mm, "radius": 6 * mm});
            skArc(sketch, "E81", {"start": v(15, 104.25) * mm, "mid": v(0, 119.25) * mm, "end": v(-15, 104.25) * mm});
            skLineSegment(sketch, "E82", {"start": v(-15, 104.25) * mm, "end": v(-15, 92.25) * mm});
            skLineSegment(sketch, "E83", {"start": v(-15, 92.25) * mm, "end": v(-33, 74.25) * mm});
            skLineSegment(sketch, "E84", {"start": v(15, 104.25) * mm, "end": v(15, 92.25) * mm});
            skLineSegment(sketch, "E85", {"start": v(15, 92.25) * mm, "end": v(33, 74.25) * mm});
            skLineSegment(sketch, "E86", {"start": v(-74.25, 0) * mm, "end": v(74.5, 0) * mm, "construction": true});
            skLineSegment(sketch, "E87.MirrorCS", {"start": v(-15, -92.25) * mm, "end": v(-33, -74.25) * mm});
            skLineSegment(sketch, "E88.MirrorCS", {"start": v(-15, -104.25) * mm, "end": v(-15, -92.25) * mm});
            skArc(sketch, "E89.MirrorCS", {"start": v(15, -104.25) * mm, "mid": v(0, -119.25) * mm, "end": v(-15, -104.25) * mm});
            skLineSegment(sketch, "E90.MirrorCS", {"start": v(15, -104.25) * mm, "end": v(15, -92.25) * mm});
            skLineSegment(sketch, "E91.MirrorCS", {"start": v(15, -92.25) * mm, "end": v(33, -74.25) * mm});
            skCircle(sketch, "E92.MirrorC", {"center": v(0, -104.25) * mm, "radius": 6 * mm});
            skLineSegment(sketch, "E93.MirrorCS", {"start": v(0, -74.25) * mm, "end": v(0, -104.25) * mm, "construction": true});
            skSolve(sketch);
        }
        {
            var Q0;
            Q0=makeQuery(id+"F16.imprint","IMPRINT",FACE,{"disambiguationData":[TD([[makeQuery(id+"F16.imprint","IMPRINT",EDGE,{"derivedFrom":makeQuery(id+"F1.opExtrude","CAP_EDGE",EDGE,{"disambiguationData":[OSD([sQuery(id+"F0.wireOp",EDGE,"E1.bottom")])],"isStart":true})}),1.0]])]});
            var Q1;
            Q1=makeQuery(id+"F17.imprint","IMPRINT",FACE,{"disambiguationData":[TD([[makeQuery(id+"F17.imprint","IMPRINT",EDGE,{"derivedFrom":sQuery(id+"F17.wireOp",EDGE,"E80")}),-1.0]])]});
            var Q2;
            {var subQ0=sQuery(id+"F17.wireOp",EDGE,"E87.MirrorCS");Q2=makeQuery(id+"F17.imprint","IMPRINT",FACE,{"disambiguationData":[TD([[makeQuery(id+"F17.imprint","IMPRINT",EDGE,{"derivedFrom":subQ0}),-1.0]])]});}
            var Q3;
            Q3=makeQuery(id+"F2.opExtrude","CAP_FACE",FACE,{"disambiguationData":[OSD([sQuery(id+"F0.wireOp",EDGE,"E12"),sQuery(id+"F0.wireOp",EDGE,"E13"),sQuery(id+"F0.wireOp",EDGE,"E14"),sQuery(id+"F0.wireOp",EDGE,"E15"),sQuery(id+"F0.wireOp",EDGE,"E17.filletArc"),sQuery(id+"F0.wireOp",EDGE,"E18.filletArc"),sQuery(id+"F0.wireOp",EDGE,"E19.filletArc"),sQuery(id+"F0.wireOp",EDGE,"E20.filletArc"),sQuery(id+"F0.wireOp",EDGE,"E25.0"),sQuery(id+"F0.wireOp",EDGE,"E25.1"),sQuery(id+"F0.wireOp",EDGE,"E25.2"),sQuery(id+"F0.wireOp",EDGE,"E25.3"),sQuery(id+"F0.wireOp",EDGE,"E25.4"),sQuery(id+"F0.wireOp",EDGE,"E25.5"),sQuery(id+"F0.wireOp",EDGE,"E25.6"),sQuery(id+"F0.wireOp",EDGE,"E25.7")])],"isStart":false});
            extrude(context, id + "F18", {"entities" : qUnion([Q0, Q1, Q2]), "operationType" : NewBodyOperationType.ADD, "endBound" : BoundingType.UP_TO_SURFACE, "endBoundEntityFace" : qUnion([Q3]), "depth" : 25 * mm});
        }
    });
